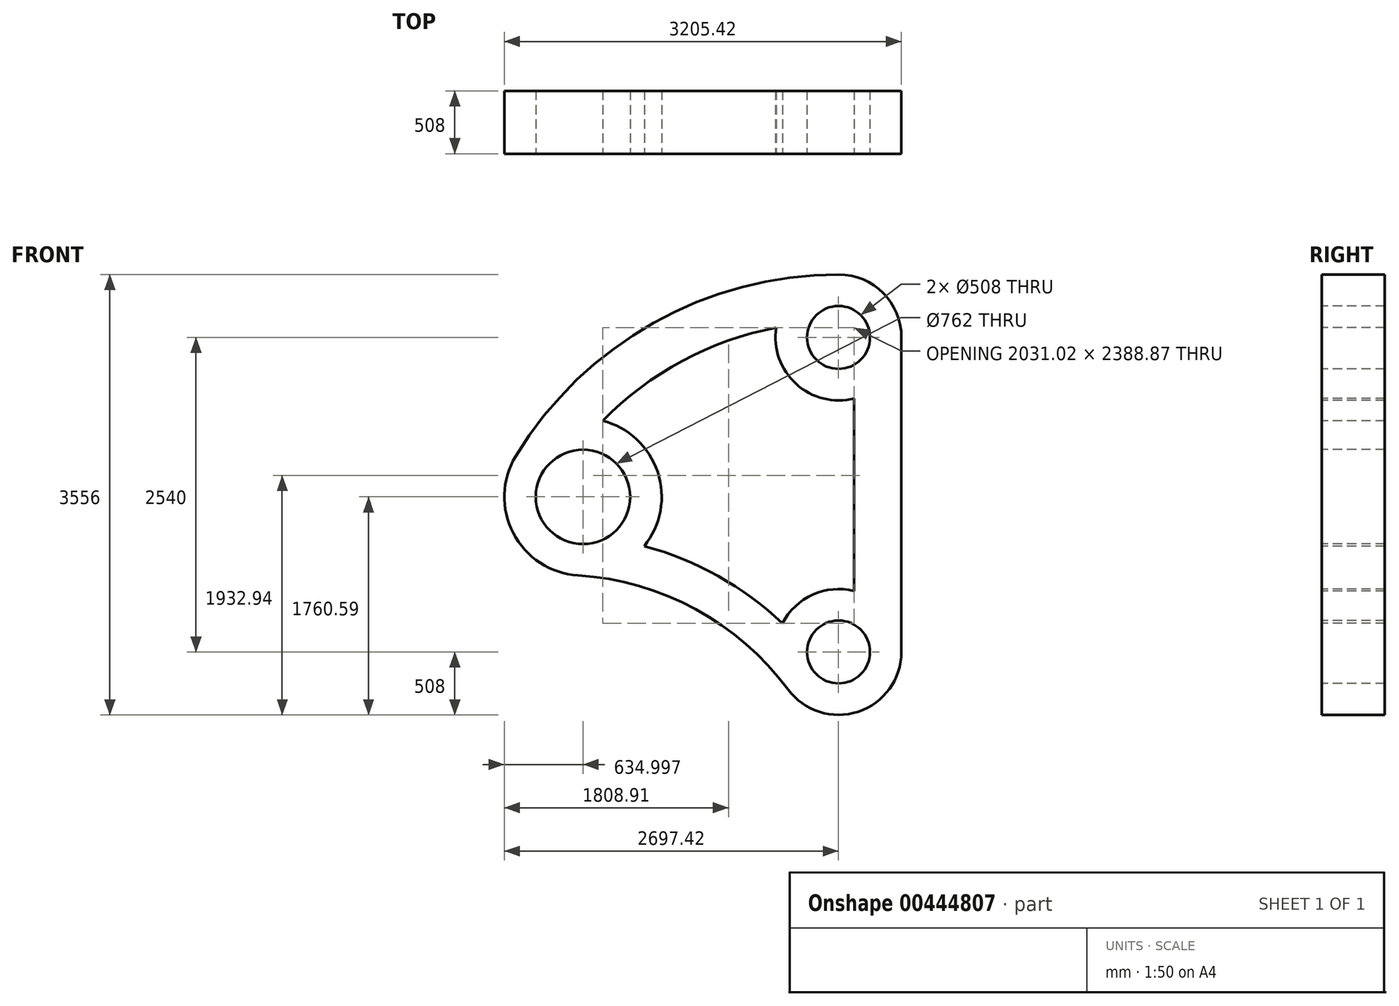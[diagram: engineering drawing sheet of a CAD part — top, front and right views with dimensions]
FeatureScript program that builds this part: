
annotation { "Feature Type Name" : "Feature", "Feature Type Description" : "" }
export const myFeature = defineFeature(function(context is Context, id is Id, definition is map)
    precondition{}
    {
        {
            var Q0;
            Q0=qCreatedBy(makeId("Front.planeOp"),FACE);
            var sketch = newSketch(context, id + "F0", { "sketchPlane" : qUnion([Q0])});
            skArc(sketch, "E0", {"start": v(-501.76, 79.38) * mm, "mid": v(-341.6, -376) * mm, "end": v(127, -491.87) * mm});
            skCircle(sketch, "E1", {"center": v(0, 0) * mm, "radius": 254 * mm});
            skArc(sketch, "E2", {"start": v(127, -2048.13) * mm, "mid": v(-208.8, -2076.9) * mm, "end": v(-452.7, -2309.5) * mm});
            skCircle(sketch, "E3", {"center": v(0, -2540) * mm, "radius": 254 * mm});
            skLineSegment(sketch, "E4", {"start": v(508, 0) * mm, "end": v(508, -2540) * mm});
            skCircle(sketch, "E5", {"center": v(-2062.42, -1287.4) * mm, "radius": 381 * mm});
            skArc(sketch, "E6", {"start": v(-2605.17, -957.78) * mm, "mid": v(-2625.33, -1581.29) * mm, "end": v(-2102.2, -1921.16) * mm});
            skArc(sketch, "E7", {"start": v(-408.26, -2842.3) * mm, "mid": v(-1153.36, -2194.4) * mm, "end": v(-2102.2, -1921.16) * mm});
            skArc(sketch, "E8", {"start": v(-2603.33, -1620.04) * mm, "mid": v(-2625.26, -1623.18) * mm, "end": v(-2647.16, -1626.5) * mm});
            skArc(sketch, "E9.trimOffspring", {"start": v(101.46, -5338.51) * mm, "mid": v(103.03, -5335.28) * mm, "end": v(104.58, -5332.04) * mm});
            skArc(sketch, "E10.trimOffspring", {"start": v(-2735.19, -1969.75) * mm, "mid": v(-2738.59, -1970.5) * mm, "end": v(-2741.99, -1971.25) * mm});
            skArc(sketch, "E11.trimOffspring", {"start": v(-2628.72, -1574.7) * mm, "mid": v(-2638.07, -1600.55) * mm, "end": v(-2647.16, -1626.5) * mm});
            skArc(sketch, "E12.trimOffspring", {"start": v(-2624.76, -1582.37) * mm, "mid": v(-2632.5, -1603.85) * mm, "end": v(-2640.07, -1625.4) * mm});
            skArc(sketch, "E13.trimOffspring", {"start": v(0, 508) * mm, "mid": v(-1494.6, 116.4) * mm, "end": v(-2605.17, -957.78) * mm});
            skArc(sketch, "E14.trimOffspring", {"start": v(-452.7, -2309.5) * mm, "mid": v(-971.19, -1927.95) * mm, "end": v(-1567.36, -1685.08) * mm});
            skArc(sketch, "E15.trimOffspring", {"start": v(-501.76, 79.38) * mm, "mid": v(-1260.26, -189.55) * mm, "end": v(-1904.02, -672.49) * mm});
            skLineSegment(sketch, "E16.trimOffspring", {"start": v(127, -491.87) * mm, "end": v(127, -2048.13) * mm});
            skArc(sketch, "E17.trimOffspring", {"start": v(508, 0) * mm, "mid": v(359.21, 359.21) * mm, "end": v(0, 508) * mm});
            skArc(sketch, "E18.trimOffspring", {"start": v(-408.26, -2842.3) * mm, "mid": v(159.17, -3022.42) * mm, "end": v(508, -2540) * mm});
            skArc(sketch, "E19.trimOffspring", {"start": v(-1567.36, -1685.08) * mm, "mid": v(-1459.85, -1087.08) * mm, "end": v(-1904.02, -672.49) * mm});
            skSolve(sketch);
        }
        {
            var Q0;
            Q0=makeQuery(id+"F0.imprint","IMPRINT",FACE,{"disambiguationData":[TD([[makeQuery(id+"F0.imprint","IMPRINT",EDGE,{"derivedFrom":sQuery(id+"F0.wireOp",EDGE,"E0")}),1.0]])]});
            extrude(context, id + "F1", {"entities" : qUnion([Q0]), "oppositeDirection" : true, "depth" : 508 * mm});
        }
    });
